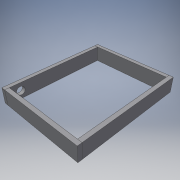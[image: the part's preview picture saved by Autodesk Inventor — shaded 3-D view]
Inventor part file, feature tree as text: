
AUTODESK INVENTOR PART (.ipt)
format: ipt  version: 2016 (Build 200138000, 138)  size: 168,960 bytes
history: native  units: in
note: dims shown in document units (in); Inventor stores cm internally (conversion verified against a paired STEP export)
features: sketch x6, split x4, extrude x2, boolean_combine x2, hole x1
ambient origin geometry x8: Origin, YZ Plane, XZ Plane, XY Plane, X Axis, Y Axis, Z Axis, Center Point
bodies: Solid1 (feature_tree), Solid2 (feature_tree), Solid3 (feature_tree), Solid4 (feature_tree), Solid5 (feature_tree), Solid6 (feature_tree), Solid7 (feature_tree), Solid8 (feature_tree), Solid9 (feature_tree)
feature tree (15):
  extrude  "Extrusion1"  Depth=16.0in
  extrude  "Extrusion2"  Depth=2.8in TaperAngle=0.0deg
  split  "Split1"
  split  "Split2"
  split  "Split3"
  split  "Split4"
  boolean_combine  "Combine1"
  boolean_combine  "Combine2"
  hole  "Hole1"  [1 undecoded]
  sketch  "Sketch1"  dims[d0=20.0in d1=16.0in]
  sketch  "Sketch2"  dims[d2=2.8in d3=0.0in d7=2.8in d8=0.0in]
  sketch  "Sketch4"  dims[d9=1.5in d10=2.5in]
  sketch  "Sketch5"  dims[d11=1.5in d12=0.75in d13=0.375in d14=0.25in d15=0.5635in d16=1.0in d17=0.8108in]
  sketch  "Sketch6"  dims[d18=0.75in]
  sketch  "Sketch7"  dims[d19=0.75in d20=0.75in d21=0.75in]
note: 1 required parameter value undecoded (feature->parameter linkage not recoverable at this tier; creation-order binding heuristic only, values carry confidence <= 0.55)
